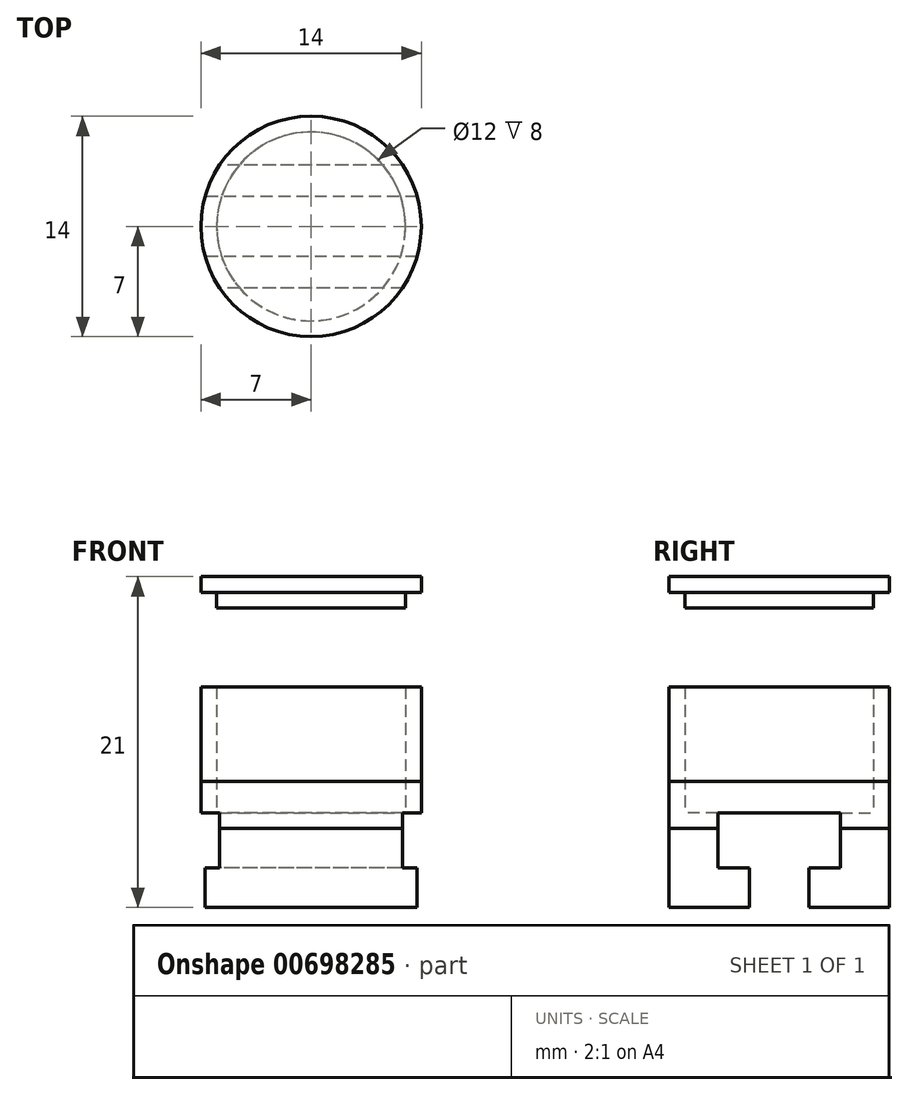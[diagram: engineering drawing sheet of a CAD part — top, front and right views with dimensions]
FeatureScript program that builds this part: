
annotation { "Feature Type Name" : "Feature", "Feature Type Description" : "" }
export const myFeature = defineFeature(function(context is Context, id is Id, definition is map)
    precondition{}
    {
        {
            var Q0;
            Q0=qCreatedBy(makeId("Top.planeOp"),FACE);
            var sketch = newSketch(context, id + "F0", { "sketchPlane" : qUnion([Q0])});
            skCircle(sketch, "E0", {"center": v(0, 0) * mm, "radius": 7 * mm});
            skSolve(sketch);
        }
        {
            var Q0;
            Q0=qSketchRegion(id+"F0",true);
            extrude(context, id + "F1", {"entities" : qUnion([Q0]), "depth" : 9 * mm, "offsetDistance" : 25 * mm});
        }
        {
            var Q0;
            Q0=makeQuery(id+"F1.opExtrude","CAP_FACE",FACE,{"disambiguationData":[OSD([sQuery(id+"F0.wireOp",EDGE,"E0")])],"isStart":false});
            shell(context, id + "F2", {"entities" : qUnion([Q0]), "thickness" : 1 * mm});
        }
        {
            var Q0;
            Q0=qCreatedBy(makeId("Top.planeOp"),FACE);
            cPlane(context, id + "F3", {"entities" : qUnion([Q0]), "cplaneType" : CPlaneType.OFFSET, "offset" : 15 * mm, "width" : 150 * mm, "height" : 150 * mm});
        }
        {
            var Q0;
            Q0=qCreatedBy(id+"F3.planeOp",FACE);
            var sketch = newSketch(context, id + "F4", { "sketchPlane" : qUnion([Q0])});
            skCircle(sketch, "E1.0", {"center": v(0, 0) * mm, "radius": 6 * mm});
            skCircle(sketch, "E2.0", {"center": v(0, 0) * mm, "radius": 7 * mm});
            skSolve(sketch);
        }
        {
            var Q0;
            Q0=makeQuery(id+"F4.imprint","IMPRINT",FACE,{"disambiguationData":[TD([[makeQuery(id+"F4.imprint","IMPRINT",EDGE,{"derivedFrom":sQuery(id+"F4.wireOp",EDGE,"E1.0")}),1.0]])]});
            extrude(context, id + "F5", {"entities" : qUnion([Q0]), "oppositeDirection" : true, "depth" : 1 * mm, "offsetDistance" : 25 * mm});
        }
        {
            var Q0;
            Q0=qSketchRegion(id+"F4",true);
            var Q1;
            Q1=makeQuery(id+"F5.opExtrude","CAP_FACE",FACE,{"disambiguationData":[OSD([sQuery(id+"F4.wireOp",EDGE,"E1.0")])],"isStart":true});
            extrude(context, id + "F6", {"entities" : qUnion([Q0, Q1]), "operationType" : NewBodyOperationType.ADD, "depth" : 1 * mm, "offsetDistance" : 25 * mm});
        }
        {
            var Q0;
            Q0=makeQuery(id+"F1.opExtrude","CAP_FACE",FACE,{"disambiguationData":[OSD([sQuery(id+"F0.wireOp",EDGE,"E0")])],"isStart":true});
            extrude(context, id + "F7", {"entities" : qUnion([Q0]), "depth" : 5 * mm, "offsetDistance" : 25 * mm, "hasSecondDirection" : true, "secondDirectionOppositeDirection" : true, "secondDirectionDepth" : 3 * mm});
        }
        {
            var Q0;
            Q0=makeQuery(id+"F1.opExtrude","CAP_FACE",FACE,{"disambiguationData":[OSD([sQuery(id+"F0.wireOp",EDGE,"E0")])],"isStart":true});
            var sketch = newSketch(context, id + "F8", { "sketchPlane" : qUnion([Q0])});
            skCircle(sketch, "E3", {"center": v(0, 0) * mm, "radius": 1.8 * mm});
            skSolve(sketch);
        }
        {
            var Q0;
            Q0=qCreatedBy(makeId("Right.planeOp"),FACE);
            var sketch = newSketch(context, id + "F9", { "sketchPlane" : qUnion([Q0])});
            skLineSegment(sketch, "E4.0", {"start": v(-7, -5) * mm, "end": v(-1.9, -5) * mm, "construction": true});
            skLineSegment(sketch, "E5.right", {"start": v(0, -5) * mm, "end": v(0, -4.88) * mm, "construction": true});
            skLineSegment(sketch, "E6.right", {"start": v(0, -4.88) * mm, "end": v(0, -5) * mm});
            skLineSegment(sketch, "E7.MirrorCS", {"start": v(-3.9, 1) * mm, "end": v(-3.9, -1.5) * mm});
            skLineSegment(sketch, "E8.MirrorCS", {"start": v(-1.9, -2.5) * mm, "end": v(-3.9, -2.5) * mm});
            skLineSegment(sketch, "E9.MirrorCS", {"start": v(-1.9, -5) * mm, "end": v(-1.9, -2.5) * mm, "construction": true});
            skLineSegment(sketch, "E10", {"start": v(-1.9, -2.5) * mm, "end": v(-1.9, -5) * mm});
            skPoint(sketch, "E11.orphan", {"position": v(0, -2.5) * mm});
            skLineSegment(sketch, "E12", {"start": v(-3.9, 1) * mm, "end": v(-3.9, -2.5) * mm});
            skLineSegment(sketch, "E13", {"start": v(0, -5) * mm, "end": v(0, 2.95) * mm, "construction": true});
            skLineSegment(sketch, "E14.MirrorCS", {"start": v(1.9, -2.5) * mm, "end": v(1.9, -5) * mm});
            skLineSegment(sketch, "E15.MirrorCS", {"start": v(3.9, 1) * mm, "end": v(3.9, -1.5) * mm});
            skLineSegment(sketch, "E16.MirrorCS", {"start": v(3.9, 1) * mm, "end": v(3.9, -2.5) * mm});
            skLineSegment(sketch, "E17.MirrorCS", {"start": v(1.9, -2.5) * mm, "end": v(3.9, -2.5) * mm});
            skLineSegment(sketch, "E18.MirrorCS", {"start": v(1.9, -5) * mm, "end": v(1.9, -2.5) * mm, "construction": true});
            skLineSegment(sketch, "E19", {"start": v(-3.9, 1) * mm, "end": v(3.9, 1) * mm});
            skLineSegment(sketch, "E20", {"start": v(-1.9, -5) * mm, "end": v(1.9, -5) * mm});
            skSolve(sketch);
        }
        {
            var Q0;
            Q0 = qSketchRegion(id + "F9", true);
            extrude(context, id + "F10", {"entities" : qUnion([Q0]), "operationType" : NewBodyOperationType.REMOVE, "depth" : 25 * mm, "offsetDistance" : 25 * mm, "hasSecondDirection" : true, "secondDirectionOppositeDirection" : true, "secondDirectionDepth" : 25 * mm});
        }
    });
